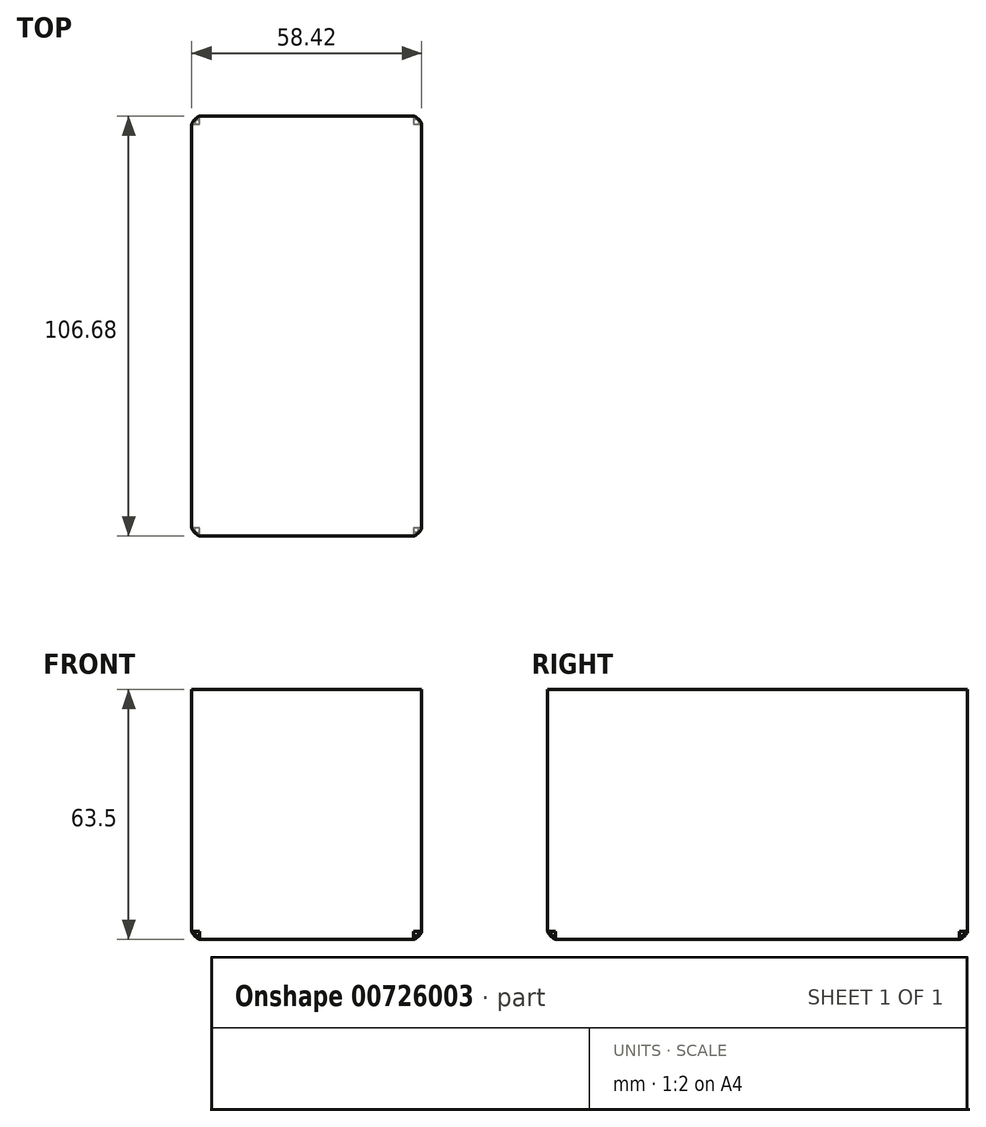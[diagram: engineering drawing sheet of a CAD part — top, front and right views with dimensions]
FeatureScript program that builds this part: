
annotation { "Feature Type Name" : "Feature", "Feature Type Description" : "" }
export const myFeature = defineFeature(function(context is Context, id is Id, definition is map)
    precondition{}
    {
        {
            var Q0;
            Q0=qCreatedBy(makeId("Right.planeOp"),FACE);
            var sketch = newSketch(context, id + "F0", { "sketchPlane" : qUnion([Q0])});
            skLineSegment(sketch, "E0.bottom", {"start": v(53.34, -31.75) * mm, "end": v(-53.34, -31.75) * mm});
            skLineSegment(sketch, "E0.top", {"start": v(53.34, 31.75) * mm, "end": v(-53.34, 31.75) * mm});
            skLineSegment(sketch, "E0.left", {"start": v(53.34, -31.75) * mm, "end": v(53.34, 31.75) * mm});
            skLineSegment(sketch, "E0.right", {"start": v(-53.34, -31.75) * mm, "end": v(-53.34, 31.75) * mm});
            skPoint(sketch, "E0.middle", {"position": v(0, 0) * mm});
            skSolve(sketch);
        }
        {
            var Q0;
            Q0=makeQuery(id+"F0.imprint","IMPRINT",FACE,{"disambiguationData":[TD([[makeQuery(id+"F0.imprint","IMPRINT",EDGE,{"derivedFrom":sQuery(id+"F0.wireOp",EDGE,"E0.bottom")}),-1.0]])]});
            extrude(context, id + "F1", {"entities" : qUnion([Q0]), "endBound" : BoundingType.SYMMETRIC, "depth" : 58.42 * mm, "offsetDistance" : 25.4 * mm});
        }
        {
            var Q0;
            Q0=makeQuery(id+"F1.opExtrude","CAP_EDGE",EDGE,{"disambiguationData":[OSD([sQuery(id+"F0.wireOp",EDGE,"E0.bottom")])],"isStart":false});
            var Q1;
            Q1=makeQuery(id+"F1.opExtrude","SWEPT_EDGE",EDGE,{"disambiguationData":[OSD([sQuery(id+"F0.wireOp",EDGE,"E0.bottom"),sQuery(id+"F0.wireOp",EDGE,"E0.right")])]});
            var Q2;
            Q2=makeQuery(id+"F1.opExtrude","CAP_EDGE",EDGE,{"disambiguationData":[OSD([sQuery(id+"F0.wireOp",EDGE,"E0.bottom")])],"isStart":true});
            var Q3;
            Q3=makeQuery(id+"F1.opExtrude","SWEPT_EDGE",EDGE,{"disambiguationData":[OSD([sQuery(id+"F0.wireOp",EDGE,"E0.bottom"),sQuery(id+"F0.wireOp",EDGE,"E0.left")])]});
            var Q4;
            Q4=makeQuery(id+"F1.opExtrude","CAP_EDGE",EDGE,{"disambiguationData":[OSD([sQuery(id+"F0.wireOp",EDGE,"E0.right")])],"isStart":false});
            var Q5;
            Q5=makeQuery(id+"F1.opExtrude","CAP_EDGE",EDGE,{"disambiguationData":[OSD([sQuery(id+"F0.wireOp",EDGE,"E0.right")])],"isStart":true});
            var Q6;
            Q6=makeQuery(id+"F1.opExtrude","CAP_EDGE",EDGE,{"disambiguationData":[OSD([sQuery(id+"F0.wireOp",EDGE,"E0.left")])],"isStart":false});
            var Q7;
            Q7=makeQuery(id+"F1.opExtrude","CAP_EDGE",EDGE,{"disambiguationData":[OSD([sQuery(id+"F0.wireOp",EDGE,"E0.left")])],"isStart":true});
            fillet(context, id + "F2", {"entities" : qUnion([Q0, Q1, Q2, Q3, Q4, Q5, Q6, Q7]), "radius" : 2.03 * mm, "tangentPropagation" : true, "rho" : .2, "crossSection" : FilletCrossSection.CONIC, "allowEdgeOverflow" : false});
        }
    });
